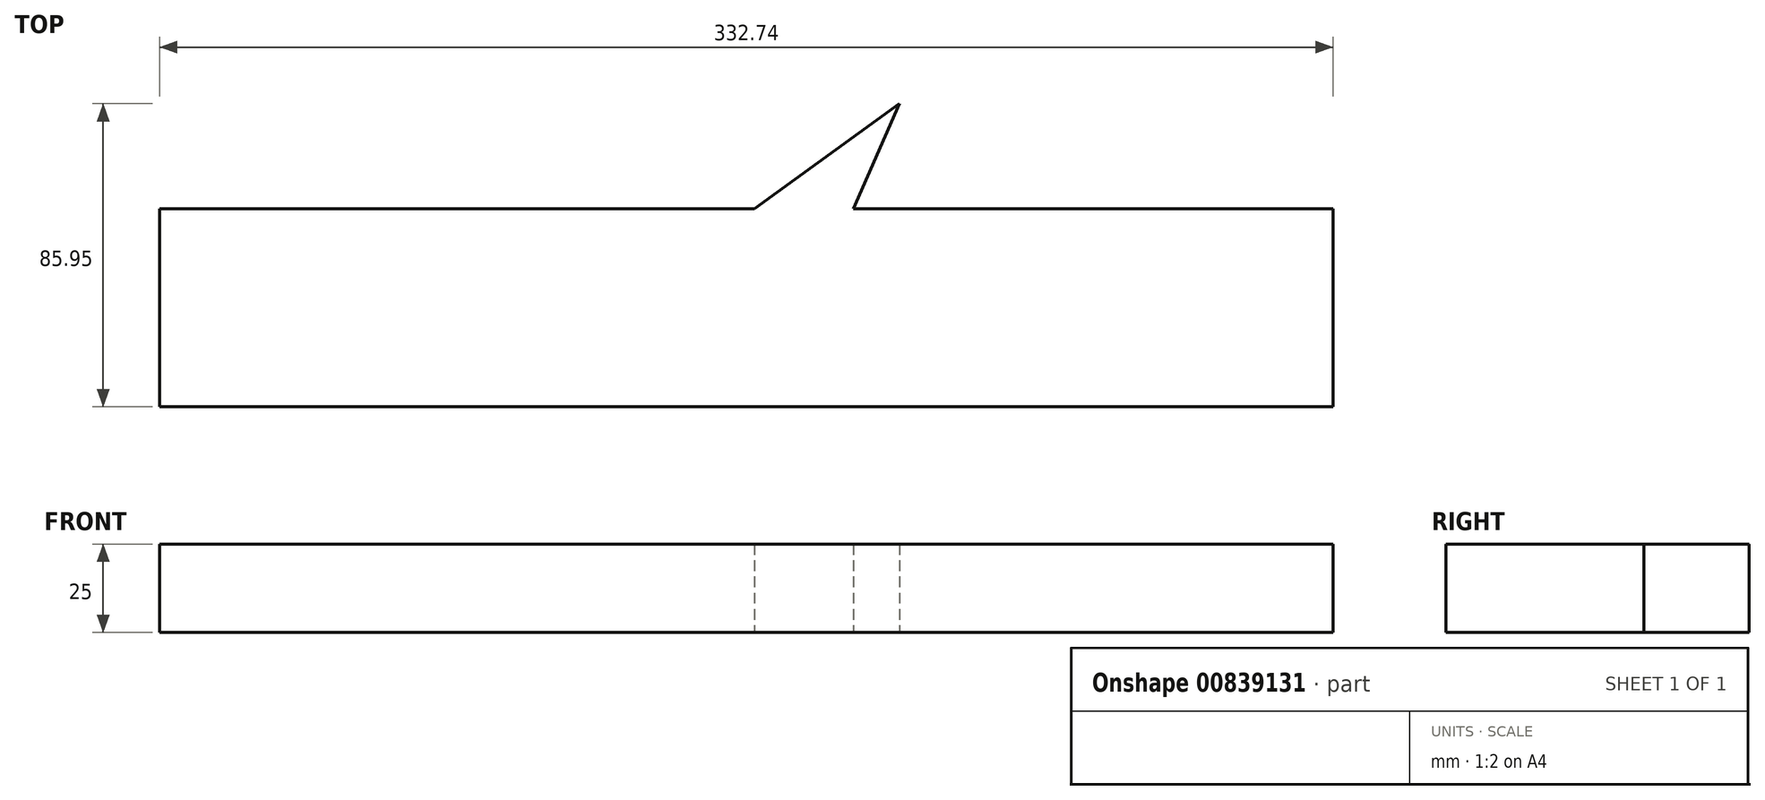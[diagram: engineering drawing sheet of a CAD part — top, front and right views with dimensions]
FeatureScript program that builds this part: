
annotation { "Feature Type Name" : "Feature", "Feature Type Description" : "" }
export const myFeature = defineFeature(function(context is Context, id is Id, definition is map)
    precondition{}
    {
        {
            var Q0;
            Q0=qCreatedBy(makeId("Top.planeOp"),FACE);
            var sketch = newSketch(context, id + "F0", { "sketchPlane" : qUnion([Q0])});
            skLineSegment(sketch, "E0", {"start": v(-169.34, -77.23) * mm, "end": v(66.43, 93.63) * mm});
            skLineSegment(sketch, "E1", {"start": v(66.43, 93.63) * mm, "end": v(29.58, 9.32) * mm});
            skLineSegment(sketch, "E2.bottom", {"start": v(-143.37, 63.82) * mm, "end": v(189.37, 63.82) * mm});
            skLineSegment(sketch, "E2.top", {"start": v(-143.37, 7.68) * mm, "end": v(189.37, 7.68) * mm});
            skLineSegment(sketch, "E2.left", {"start": v(-143.37, 63.82) * mm, "end": v(-143.37, 7.68) * mm});
            skLineSegment(sketch, "E2.right", {"start": v(189.37, 63.82) * mm, "end": v(189.37, 7.68) * mm});
            skSolve(sketch);
        }
        {
            var Q0;
            Q0 = qSketchRegion(id + "F0", true);
            extrude(context, id + "F1", {"entities" : qUnion([Q0]), "depth" : 25 * mm, "offsetDistance" : 25 * mm});
        }
    });
